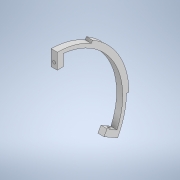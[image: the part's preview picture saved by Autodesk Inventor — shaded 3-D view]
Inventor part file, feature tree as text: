
AUTODESK INVENTOR PART (.ipt)
format: ipt  version: 2021 (Build 250183000, 183)  size: 155,648 bytes
history: native  units: in
note: dims shown in document units (in); Inventor stores cm internally (conversion verified against a paired STEP export)
features: hole x2, sketch x2, extrude x1, other x1
ambient origin geometry x8: Origin, YZ Plane, XZ Plane, XY Plane, X Axis, Y Axis, Z Axis, Center Point
bodies: Body1 (feature_tree)
feature tree (6):
  extrude  "Extrusion2"  TaperAngle=30.0deg  [1 undecoded]
  hole  "Hole1"  [1 undecoded]
  hole  "Hole2"  [1 undecoded]
  other  "Part"
  sketch  "Sketch5"  dims[d29=2.375in d32=30.0deg]
  sketch  "Sketch6"  dims[d34=2.175in d35=0.2in d37=60.0deg d38=2.175in d42=0.59in d44=0.4134in d45=2.2963in d46=0.2in d47=0.0in d48=0.3346in d49=0.096in d50=0.75in d51=0.172in d52=0.25in d53=0.5635in d54=0.484in d55=0.8108in d56=0.3346in d57=0.096in d58=0.75in d59=0.172in d60=0.25in d61=0.5635in d62=0.484in d63=0.8108in d64=0.0315in d33=0.0344in]
note: 3 required parameter values undecoded (feature->parameter linkage not recoverable at this tier; creation-order binding heuristic only, values carry confidence <= 0.55)
